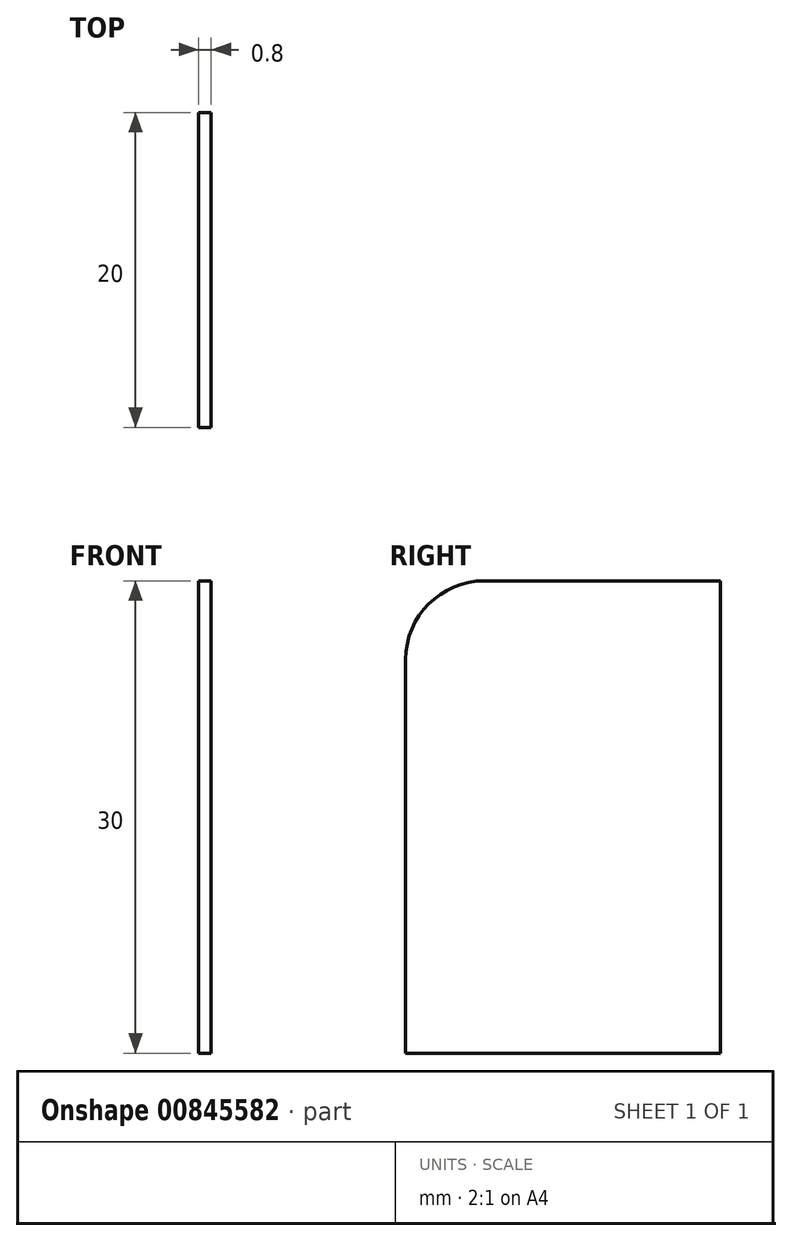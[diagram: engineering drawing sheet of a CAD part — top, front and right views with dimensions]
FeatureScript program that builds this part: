
annotation { "Feature Type Name" : "Feature", "Feature Type Description" : "" }
export const myFeature = defineFeature(function(context is Context, id is Id, definition is map)
    precondition{}
    {
        {
            var Q0;
            Q0=qCreatedBy(makeId("Right.planeOp"),FACE);
            var sketch = newSketch(context, id + "F0", { "sketchPlane" : qUnion([Q0])});
            skLineSegment(sketch, "E0", {"start": v(-9.79, 0) * mm, "end": v(-9.79, -25) * mm});
            skLineSegment(sketch, "E1", {"start": v(-9.79, -25) * mm, "end": v(10.21, -25) * mm});
            skLineSegment(sketch, "E2", {"start": v(10.21, -25) * mm, "end": v(10.21, 5) * mm});
            skLineSegment(sketch, "E3", {"start": v(10.21, 5) * mm, "end": v(-4.79, 5) * mm});
            skArc(sketch, "E4", {"start": v(-9.79, 0) * mm, "mid": v(-8.32, 3.54) * mm, "end": v(-4.79, 5) * mm});
            skSolve(sketch);
        }
        {
            var Q0;
            Q0=makeQuery(id+"F0.imprint","IMPRINT",FACE,{"disambiguationData":[TD([[makeQuery(id+"F0.imprint","IMPRINT",EDGE,{"derivedFrom":sQuery(id+"F0.wireOp",EDGE,"E0")}),1.0]])]});
            extrude(context, id + "F1", {"entities" : qUnion([Q0]), "depth" : 0.8 * mm, "offsetDistance" : 25 * mm});
        }
    });
